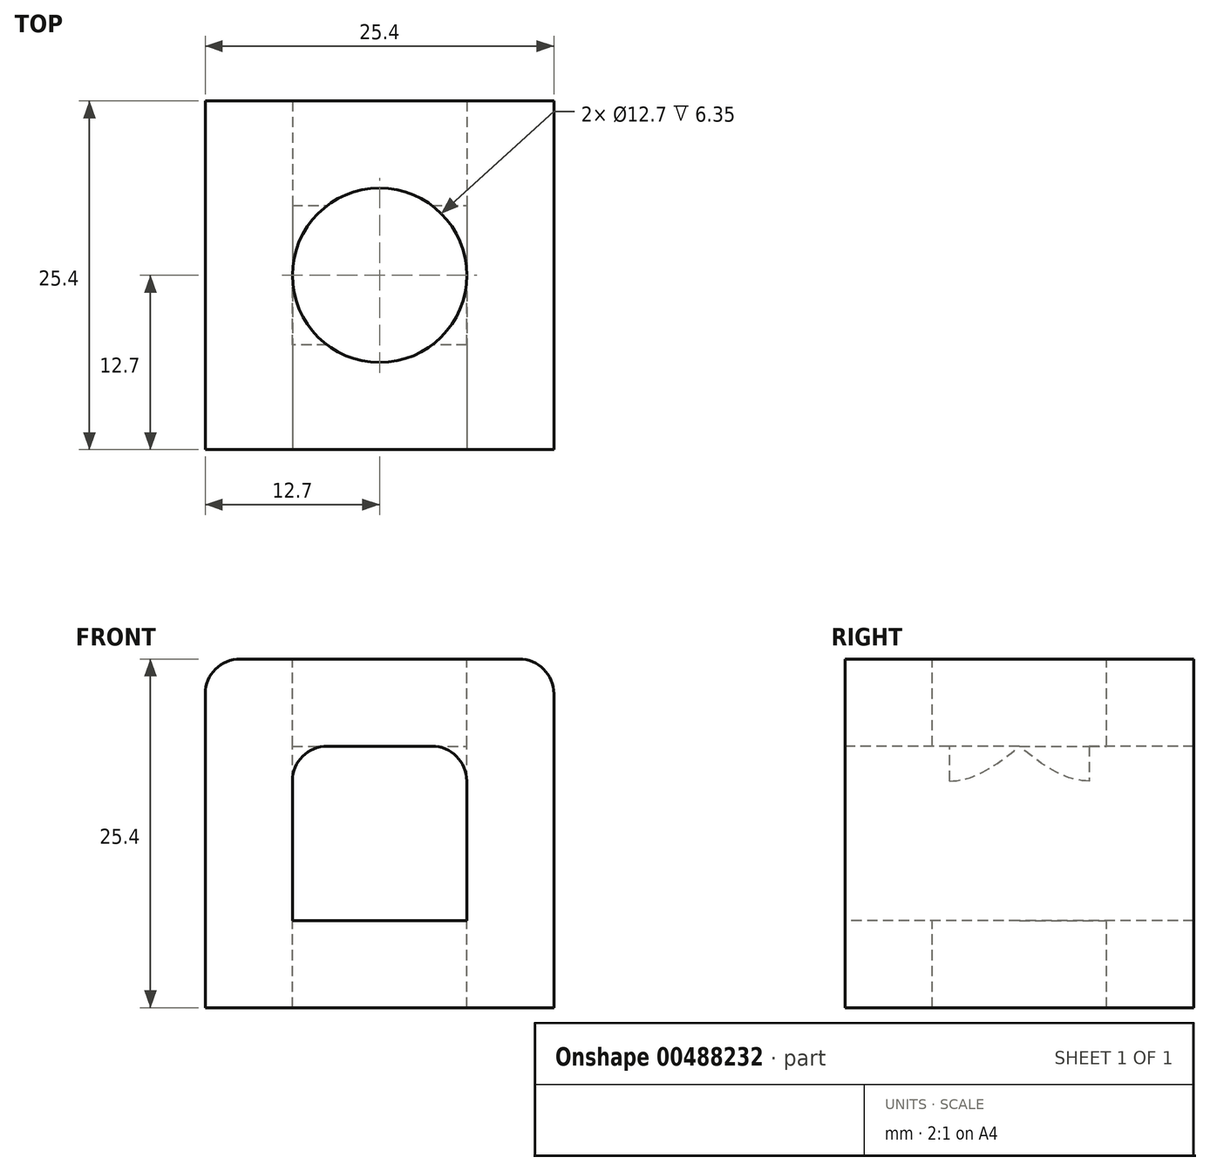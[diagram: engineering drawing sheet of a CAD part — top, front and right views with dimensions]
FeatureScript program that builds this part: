
annotation { "Feature Type Name" : "Feature", "Feature Type Description" : "" }
export const myFeature = defineFeature(function(context is Context, id is Id, definition is map)
    precondition{}
    {
        {
            var Q0;
            Q0=qCreatedBy(makeId("Top.planeOp"),FACE);
            var sketch = newSketch(context, id + "F0", { "sketchPlane" : qUnion([Q0])});
            skLineSegment(sketch, "E0.bottom", {"start": v(12.7, -12.7) * mm, "end": v(-12.7, -12.7) * mm});
            skLineSegment(sketch, "E0.top", {"start": v(12.7, 12.7) * mm, "end": v(-12.7, 12.7) * mm});
            skLineSegment(sketch, "E0.left", {"start": v(12.7, -12.7) * mm, "end": v(12.7, 12.7) * mm});
            skLineSegment(sketch, "E0.right", {"start": v(-12.7, -12.7) * mm, "end": v(-12.7, 12.7) * mm});
            skPoint(sketch, "E0.middle", {"position": v(0, 0) * mm});
            skSolve(sketch);
        }
        {
            var Q0;
            Q0 = qSketchRegion(id + "F0", true);
            extrude(context, id + "F1", {"entities" : qUnion([Q0]), "depth" : 25.4 * mm});
        }
        {
            var Q0;
            Q0=makeQuery(id+"F1.opExtrude","CAP_FACE",FACE,{"disambiguationData":[OSD([sQuery(id+"F0.wireOp",EDGE,"E0.bottom"),sQuery(id+"F0.wireOp",EDGE,"E0.top"),sQuery(id+"F0.wireOp",EDGE,"E0.left"),sQuery(id+"F0.wireOp",EDGE,"E0.right")])],"isStart":false});
            var sketch = newSketch(context, id + "F2", { "sketchPlane" : qUnion([Q0])});
            skCircle(sketch, "E1", {"center": v(0, 0) * mm, "radius": 6.35 * mm});
            skSolve(sketch);
        }
        {
            var Q0;
            Q0 = qSketchRegion(id + "F2", true);
            extrude(context, id + "F3", {"entities" : qUnion([Q0]), "operationType" : NewBodyOperationType.REMOVE, "oppositeDirection" : true, "depth" : 38.1 * mm});
        }
        {
            var Q0;
            Q0=makeQuery(id+"F1.opExtrude","CAP_EDGE",EDGE,{"disambiguationData":[OSD([sQuery(id+"F0.wireOp",EDGE,"E0.left")])],"isStart":false});
            var Q1;
            Q1=makeQuery(id+"F1.opExtrude","CAP_EDGE",EDGE,{"disambiguationData":[OSD([sQuery(id+"F0.wireOp",EDGE,"E0.right")])],"isStart":false});
            fillet(context, id + "F4", {"entities" : qUnion([Q0, Q1]), "radius" : 2.54 * mm, "tangentPropagation" : true, "allowEdgeOverflow" : false});
        }
        {
            var Q0;
            Q0=makeQuery(id+"F1.opExtrude","SWEPT_FACE",FACE,{"disambiguationData":[OSD([sQuery(id+"F0.wireOp",EDGE,"E0.bottom")])]});
            var sketch = newSketch(context, id + "F5", { "sketchPlane" : qUnion([Q0])});
            skLineSegment(sketch, "E2.bottom", {"start": v(6.35, 6.35) * mm, "end": v(-6.35, 6.35) * mm});
            skLineSegment(sketch, "E2.top", {"start": v(6.35, 19.05) * mm, "end": v(-6.35, 19.05) * mm});
            skLineSegment(sketch, "E2.left", {"start": v(6.35, 6.35) * mm, "end": v(6.35, 19.05) * mm});
            skLineSegment(sketch, "E2.right", {"start": v(-6.35, 6.35) * mm, "end": v(-6.35, 19.05) * mm});
            skPoint(sketch, "E2.middle", {"position": v(0, 12.7) * mm});
            skSolve(sketch);
        }
        {
            var Q0;
            Q0 = qSketchRegion(id + "F5", true);
            extrude(context, id + "F6", {"entities" : qUnion([Q0]), "operationType" : NewBodyOperationType.REMOVE, "oppositeDirection" : true, "depth" : 38.1 * mm});
        }
        {
            var Q0;
            {var subQ0=sQuery(id+"F5.wireOp",EDGE,"E2.top");var subQ1=sQuery(id+"F5.wireOp",EDGE,"E2.right");Q0=makeQuery(id+"F6.boolean.opBoolean","COPY",EDGE,{"disambiguationData":[TD([makeQuery(id+"F1.opExtrude","SWEPT_FACE",FACE,{"disambiguationData":[OSD([sQuery(id+"F0.wireOp",EDGE,"E0.bottom")])]})])],"derivedFrom":makeQuery(id+"F6.opExtrude","SWEPT_EDGE",EDGE,{"disambiguationData":[OSD([subQ0,subQ1])]})});}
            var Q1;
            {var subQ0=sQuery(id+"F5.wireOp",EDGE,"E2.top");var subQ1=sQuery(id+"F5.wireOp",EDGE,"E2.left");Q1=makeQuery(id+"F6.boolean.opBoolean","COPY",EDGE,{"disambiguationData":[TD([makeQuery(id+"F1.opExtrude","SWEPT_FACE",FACE,{"disambiguationData":[OSD([sQuery(id+"F0.wireOp",EDGE,"E0.bottom")])]})])],"derivedFrom":makeQuery(id+"F6.opExtrude","SWEPT_EDGE",EDGE,{"disambiguationData":[OSD([subQ0,subQ1])]})});}
            fillet(context, id + "F7", {"entities" : qUnion([Q0, Q1]), "radius" : 2.54 * mm, "tangentPropagation" : true, "allowEdgeOverflow" : false});
        }
    });
